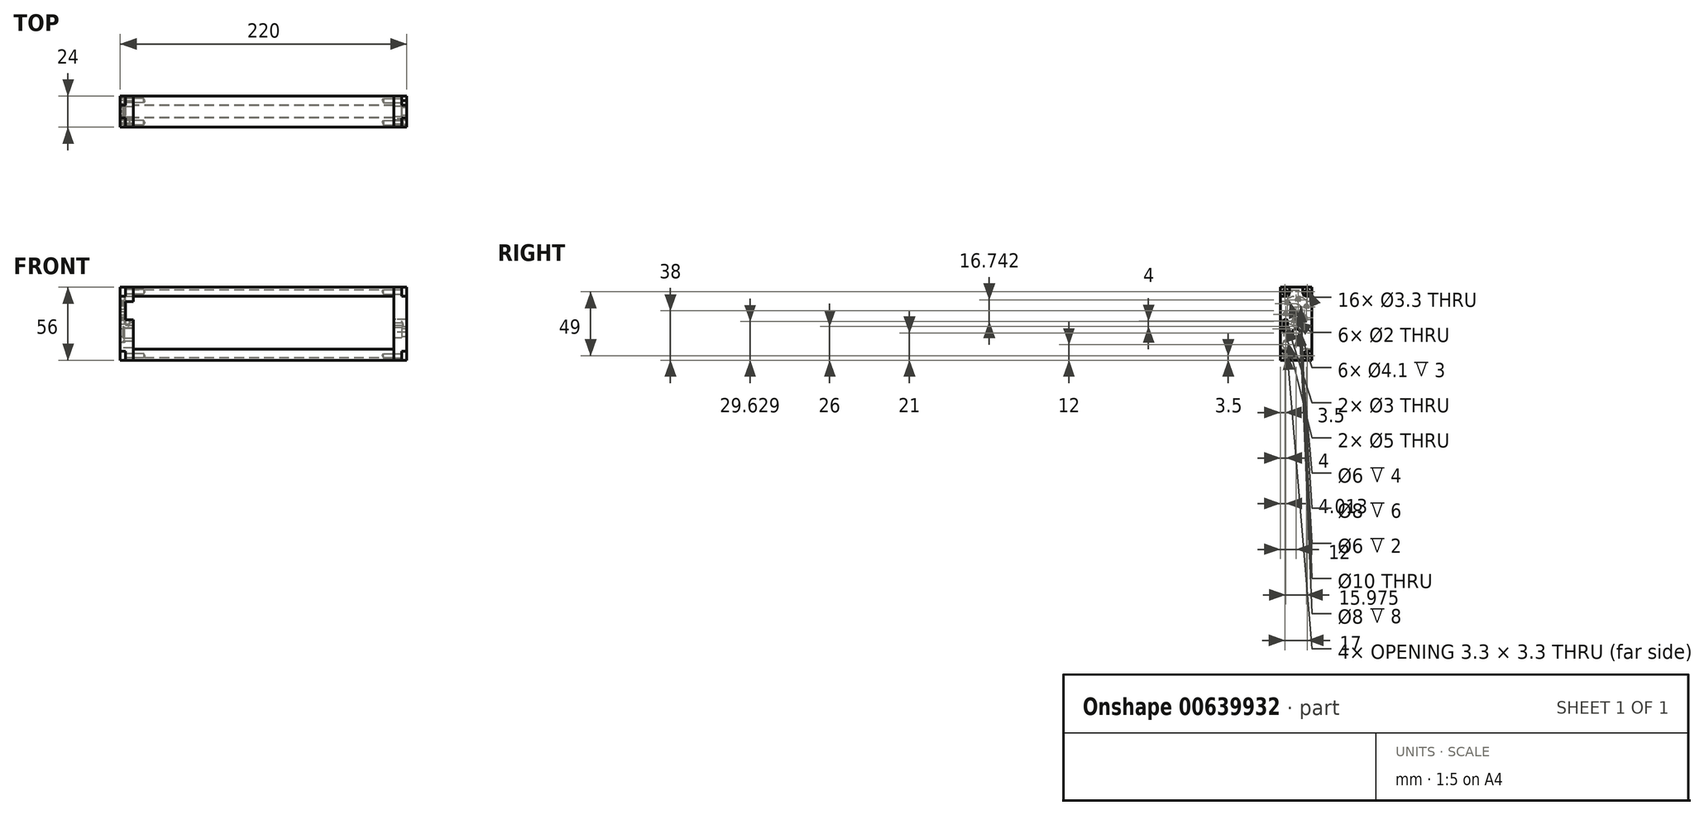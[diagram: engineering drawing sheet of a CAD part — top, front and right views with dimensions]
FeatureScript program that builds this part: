
annotation { "Feature Type Name" : "Feature", "Feature Type Description" : "" }
export const myFeature = defineFeature(function(context is Context, id is Id, definition is map)
    precondition{}
    {
        {
            var Q0;
            Q0=qCreatedBy(makeId("Right.planeOp"),FACE);
            var sketch = newSketch(context, id + "F0", { "sketchPlane" : qUnion([Q0])});
            skLineSegment(sketch, "E0.bottom", {"start": v(0, 0) * mm, "end": v(24, 0) * mm});
            skLineSegment(sketch, "E0.top", {"start": v(0, 56) * mm, "end": v(24, 56) * mm});
            skLineSegment(sketch, "E0.left", {"start": v(0, 0) * mm, "end": v(0, 56) * mm});
            skLineSegment(sketch, "E0.right", {"start": v(24, 0) * mm, "end": v(24, 56) * mm});
            skCircle(sketch, "E1", {"center": v(12, 38) * mm, "radius": 5 * mm});
            skCircle(sketch, "E2", {"center": v(12, 21) * mm, "radius": 3 * mm});
            skLineSegment(sketch, "E3", {"start": v(12, 56) * mm, "end": v(12, 0) * mm, "construction": true});
            skCircle(sketch, "E4", {"center": v(4, 12) * mm, "radius": 2.5 * mm});
            skCircle(sketch, "E5", {"center": v(4, 26) * mm, "radius": 1.5 * mm});
            skSolve(sketch);
        }
        {
            var Q0;
            Q0 = qSketchRegion(id + "F0", true);
            extrude(context, id + "F1", {"entities" : qUnion([Q0]), "depth" : 10 * mm, "offsetDistance" : 25 * mm});
        }
        {
            var Q0;
            Q0=makeQuery(id+"F1.opExtrude","CAP_FACE",FACE,{"disambiguationData":[OSD([sQuery(id+"F0.wireOp",EDGE,"E0.bottom"),sQuery(id+"F0.wireOp",EDGE,"E0.top"),sQuery(id+"F0.wireOp",EDGE,"E0.left"),sQuery(id+"F0.wireOp",EDGE,"E0.right"),sQuery(id+"F0.wireOp",EDGE,"E1"),sQuery(id+"F0.wireOp",EDGE,"E2")])],"isStart":false});
            var sketch = newSketch(context, id + "F2", { "sketchPlane" : qUnion([Q0])});
            skCircle(sketch, "E6", {"center": v(12, 38) * mm, "radius": 11.1 * mm});
            skSolve(sketch);
        }
        {
            var Q0;
            Q0 = qSketchRegion(id + "F2", true);
            extrude(context, id + "F3", {"entities" : qUnion([Q0]), "operationType" : NewBodyOperationType.REMOVE, "oppositeDirection" : true, "depth" : 6 * mm, "offsetDistance" : 25 * mm});
        }
        {
            var Q0;
            Q0=makeQuery(id+"F1.opExtrude","CAP_FACE",FACE,{"disambiguationData":[OSD([sQuery(id+"F0.wireOp",EDGE,"E0.bottom"),sQuery(id+"F0.wireOp",EDGE,"E0.top"),sQuery(id+"F0.wireOp",EDGE,"E0.left"),sQuery(id+"F0.wireOp",EDGE,"E0.right"),sQuery(id+"F0.wireOp",EDGE,"E1"),sQuery(id+"F0.wireOp",EDGE,"E2")])],"isStart":false});
            var sketch = newSketch(context, id + "F4", { "sketchPlane" : qUnion([Q0])});
            skCircle(sketch, "E7", {"center": v(12, 21) * mm, "radius": 4 * mm});
            skSolve(sketch);
        }
        {
            var Q0;
            Q0=makeQuery(id+"F4.imprint","IMPRINT",FACE,{"disambiguationData":[TD([[makeQuery(id+"F4.imprint","IMPRINT",EDGE,{"derivedFrom":sQuery(id+"F4.wireOp",EDGE,"E7")}),1.0]])]});
            extrude(context, id + "F5", {"entities" : qUnion([Q0]), "operationType" : NewBodyOperationType.REMOVE, "oppositeDirection" : true, "depth" : 8 * mm, "offsetDistance" : 25 * mm});
        }
        {
            var Q0;
            Q0=makeQuery(id+"F1.opExtrude","CAP_FACE",FACE,{"disambiguationData":[OSD([sQuery(id+"F0.wireOp",EDGE,"E0.bottom"),sQuery(id+"F0.wireOp",EDGE,"E0.top"),sQuery(id+"F0.wireOp",EDGE,"E0.left"),sQuery(id+"F0.wireOp",EDGE,"E0.right"),sQuery(id+"F0.wireOp",EDGE,"E1"),sQuery(id+"F0.wireOp",EDGE,"E2")])],"isStart":true});
            var sketch = newSketch(context, id + "F6", { "sketchPlane" : qUnion([Q0])});
            skCircle(sketch, "E8.cCircle", {"center": v(-12, 38) * mm, "radius": 8.5 * mm, "construction": true});
            skLineSegment(sketch, "E8.0", {"start": v(-19.99, 40.9) * mm, "end": v(-13.48, 46.37) * mm, "construction": true});
            skLineSegment(sketch, "E8.1", {"start": v(-13.48, 46.37) * mm, "end": v(-5.49, 43.46) * mm, "construction": true});
            skLineSegment(sketch, "E8.2", {"start": v(-5.49, 43.46) * mm, "end": v(-4.01, 35.1) * mm, "construction": true});
            skLineSegment(sketch, "E8.3", {"start": v(-4.01, 35.1) * mm, "end": v(-10.52, 29.63) * mm, "construction": true});
            skLineSegment(sketch, "E8.4", {"start": v(-10.52, 29.63) * mm, "end": v(-18.51, 32.54) * mm, "construction": true});
            skLineSegment(sketch, "E8.5", {"start": v(-18.51, 32.54) * mm, "end": v(-19.99, 40.9) * mm, "construction": true});
            skLineSegment(sketch, "E9", {"start": v(-10.52, 29.63) * mm, "end": v(-13.48, 46.37) * mm, "construction": true});
            skPoint(sketch, "E10", {"position": v(-19.99, 40.9) * mm});
            skPoint(sketch, "E11", {"position": v(-18.51, 32.54) * mm});
            skPoint(sketch, "E12", {"position": v(-10.52, 29.63) * mm});
            skPoint(sketch, "E13", {"position": v(-4.01, 35.1) * mm});
            skPoint(sketch, "E14", {"position": v(-5.49, 43.46) * mm});
            skPoint(sketch, "E15", {"position": v(-13.48, 46.37) * mm});
            skLineSegment(sketch, "E16", {"start": v(-12, 38) * mm, "end": v(-12, 0) * mm, "construction": true});
            skSolve(sketch);
        }
        {
            var Q0;
            Q0=sQuery(id+"F6.wireOp",VERTEX,"E15");
            var Q1;
            Q1=sQuery(id+"F6.wireOp",VERTEX,"E10");
            var Q2;
            Q2=sQuery(id+"F6.wireOp",VERTEX,"E11");
            var Q3;
            Q3=sQuery(id+"F6.wireOp",VERTEX,"E12");
            var Q4;
            Q4=sQuery(id+"F6.wireOp",VERTEX,"E13");
            var Q5;
            Q5=sQuery(id+"F6.wireOp",VERTEX,"E14");
            var Q6;
            Q6=makeQuery(id+"F1.opExtrude","SWEPT_BODY",BODY,{"disambiguationData":[OSD([sQuery(id+"F0.wireOp",EDGE,"E0.bottom"),sQuery(id+"F0.wireOp",EDGE,"E0.top"),sQuery(id+"F0.wireOp",EDGE,"E0.left"),sQuery(id+"F0.wireOp",EDGE,"E0.right"),sQuery(id+"F0.wireOp",EDGE,"E1"),sQuery(id+"F0.wireOp",EDGE,"E2")])]});
            hole(context, id + "F7", {"style" : HoleStyle.C_BORE, "endStyle" : HoleEndStyle.BLIND, "holeDiameter" : 2 * mm, "cBoreDiameter" : 4.1 * mm, "cBoreDepth" : 3 * mm, "majorDiameter" : 5 * mm, "holeDepth" : 10 * mm, "isTappedThrough" : true, "tappedDepth" : 7 * mm, "tapClearance" : 2, "startFromSketch" : true, "locations" : qUnion([Q0, Q1, Q2, Q3, Q4, Q5]), "scope" : qUnion([Q6])});
        }
        {
            var Q0;
            Q0=makeQuery(id+"F3.boolean.opBoolean","COPY",FACE,{"derivedFrom":makeQuery(id+"F3.opExtrude","CAP_FACE",FACE,{"disambiguationData":[OSD([sQuery(id+"F2.wireOp",EDGE,"E6")])],"isStart":false})});
            var sketch = newSketch(context, id + "F8", { "sketchPlane" : qUnion([Q0])});
            skLineSegment(sketch, "E17.bottom", {"start": v(0, 45) * mm, "end": v(24, 45) * mm});
            skLineSegment(sketch, "E17.top", {"start": v(0, 31) * mm, "end": v(24, 31) * mm});
            skLineSegment(sketch, "E17.left", {"start": v(0, 45) * mm, "end": v(0, 31) * mm});
            skLineSegment(sketch, "E17.right", {"start": v(24, 45) * mm, "end": v(24, 31) * mm});
            skLineSegment(sketch, "E18", {"start": v(12, 38) * mm, "end": v(34.16, 38) * mm, "construction": true});
            skPoint(sketch, "E18.endSnap0", {"position": v(24, 38) * mm});
            skSolve(sketch);
        }
        {
            var Q0;
            Q0 = qSketchRegion(id + "F8", true);
            extrude(context, id + "F9", {"entities" : qUnion([Q0]), "operationType" : NewBodyOperationType.REMOVE, "depth" : 25 * mm, "offsetDistance" : 25 * mm});
        }
        {
            var Q0;
            {var subQ0=sQuery(id+"F0.wireOp",EDGE,"E0.right");var subQ1=sQuery(id+"F0.wireOp",EDGE,"E0.left");var subQ2=sQuery(id+"F0.wireOp",EDGE,"E0.bottom");Q0=makeQuery(id+"F9.boolean.opBoolean","SPLIT",FACE,{"disambiguationData":[TD([makeQuery(id+"F1.opExtrude","SWEPT_FACE",FACE,{"disambiguationData":[OSD([subQ2])]})])],"derivedFrom":makeQuery(id+"F1.opExtrude","CAP_FACE",FACE,{"disambiguationData":[OSD([subQ2,sQuery(id+"F0.wireOp",EDGE,"E0.top"),subQ1,subQ0,sQuery(id+"F0.wireOp",EDGE,"E1"),sQuery(id+"F0.wireOp",EDGE,"E2")])],"isStart":false})});}
            var sketch = newSketch(context, id + "F10", { "sketchPlane" : qUnion([Q0])});
            skLineSegment(sketch, "E19.bottom", {"start": v(0, 0) * mm, "end": v(24, 0) * mm});
            skLineSegment(sketch, "E19.top", {"start": v(0, 2) * mm, "end": v(24, 2) * mm});
            skLineSegment(sketch, "E19.left", {"start": v(0, 0) * mm, "end": v(0, 2) * mm});
            skLineSegment(sketch, "E19.right", {"start": v(24, 0) * mm, "end": v(24, 2) * mm});
            skLineSegment(sketch, "E20.bottom", {"start": v(0, 2) * mm, "end": v(7.5, 2) * mm});
            skLineSegment(sketch, "E20.top", {"start": v(0, 8.5) * mm, "end": v(7.5, 8.5) * mm});
            skLineSegment(sketch, "E20.left", {"start": v(0, 2) * mm, "end": v(0, 8.5) * mm});
            skLineSegment(sketch, "E20.right", {"start": v(7.5, 2) * mm, "end": v(7.5, 8.5) * mm});
            skLineSegment(sketch, "E21.bottom", {"start": v(24, 2) * mm, "end": v(16.5, 2) * mm});
            skLineSegment(sketch, "E21.top", {"start": v(24, 8.5) * mm, "end": v(16.5, 8.5) * mm});
            skLineSegment(sketch, "E21.left", {"start": v(24, 2) * mm, "end": v(24, 8.5) * mm});
            skLineSegment(sketch, "E21.right", {"start": v(16.5, 2) * mm, "end": v(16.5, 8.5) * mm});
            skLineSegment(sketch, "E22.bottom", {"start": v(0, 56) * mm, "end": v(24, 56) * mm});
            skLineSegment(sketch, "E22.top", {"start": v(0, 54) * mm, "end": v(24, 54) * mm});
            skLineSegment(sketch, "E22.left", {"start": v(0, 56) * mm, "end": v(0, 54) * mm});
            skLineSegment(sketch, "E22.right", {"start": v(24, 56) * mm, "end": v(24, 54) * mm});
            skLineSegment(sketch, "E23.bottom", {"start": v(0, 54) * mm, "end": v(7, 54) * mm});
            skLineSegment(sketch, "E23.top", {"start": v(0, 49) * mm, "end": v(7, 49) * mm});
            skLineSegment(sketch, "E23.left", {"start": v(0, 54) * mm, "end": v(0, 49) * mm});
            skLineSegment(sketch, "E23.right", {"start": v(7, 54) * mm, "end": v(7, 49) * mm});
            skLineSegment(sketch, "E24.bottom", {"start": v(24, 54) * mm, "end": v(17, 54) * mm});
            skLineSegment(sketch, "E24.top", {"start": v(24, 49) * mm, "end": v(17, 49) * mm});
            skLineSegment(sketch, "E24.left", {"start": v(24, 54) * mm, "end": v(24, 49) * mm});
            skLineSegment(sketch, "E24.right", {"start": v(17, 54) * mm, "end": v(17, 49) * mm});
            skSolve(sketch);
        }
        {
            var Q0;
            Q0 = qSketchRegion(id + "F10", true);
            extrude(context, id + "F11", {"entities" : qUnion([Q0]), "depth" : 200 * mm, "offsetDistance" : 25 * mm});
        }
        {
            var Q0;
            Q0=qCreatedBy(makeId("Right.planeOp"),FACE);
            var sketch = newSketch(context, id + "F12", { "sketchPlane" : qUnion([Q0])});
            skLineSegment(sketch, "E25.bottom", {"start": v(20.5, 52.5) * mm, "end": v(3.5, 52.5) * mm, "construction": true});
            skLineSegment(sketch, "E25.top", {"start": v(20.5, 3.5) * mm, "end": v(3.5, 3.5) * mm, "construction": true});
            skLineSegment(sketch, "E25.left", {"start": v(20.5, 52.5) * mm, "end": v(20.5, 3.5) * mm, "construction": true});
            skLineSegment(sketch, "E25.right", {"start": v(3.5, 52.5) * mm, "end": v(3.5, 3.5) * mm, "construction": true});
            skPoint(sketch, "E26", {"position": v(20.5, 52.5) * mm});
            skPoint(sketch, "E27", {"position": v(3.5, 52.5) * mm});
            skPoint(sketch, "E28", {"position": v(3.5, 3.5) * mm});
            skPoint(sketch, "E29", {"position": v(20.5, 3.5) * mm});
            skSolve(sketch);
        }
        {
            var Q0;
            Q0=sQuery(id+"F12.wireOp",VERTEX,"E26");
            var Q1;
            Q1=sQuery(id+"F12.wireOp",VERTEX,"E27");
            var Q2;
            Q2=sQuery(id+"F12.wireOp",VERTEX,"E29");
            var Q3;
            Q3=sQuery(id+"F12.wireOp",VERTEX,"E28");
            var Q4;
            Q4=makeQuery(id+"F1.opExtrude","SWEPT_BODY",BODY,{"disambiguationData":[OSD([sQuery(id+"F0.wireOp",EDGE,"E0.bottom"),sQuery(id+"F0.wireOp",EDGE,"E0.top"),sQuery(id+"F0.wireOp",EDGE,"E0.left"),sQuery(id+"F0.wireOp",EDGE,"E0.right"),sQuery(id+"F0.wireOp",EDGE,"E1"),sQuery(id+"F0.wireOp",EDGE,"E2")])]});
            var Q5;
            Q5=makeQuery(id+"F11.opExtrude","SWEPT_BODY",BODY,{"disambiguationData":[OSD([sQuery(id+"F10.wireOp",EDGE,"E22.bottom"),sQuery(id+"F10.wireOp",EDGE,"E22.top"),sQuery(id+"F10.wireOp",EDGE,"E22.left"),sQuery(id+"F10.wireOp",EDGE,"E22.right"),sQuery(id+"F10.wireOp",EDGE,"E23.top"),sQuery(id+"F10.wireOp",EDGE,"E23.left"),sQuery(id+"F10.wireOp",EDGE,"E23.right"),sQuery(id+"F10.wireOp",EDGE,"E24.top"),sQuery(id+"F10.wireOp",EDGE,"E24.left"),sQuery(id+"F10.wireOp",EDGE,"E24.right")])]});
            var Q6;
            Q6=makeQuery(id+"F11.opExtrude","SWEPT_BODY",BODY,{"disambiguationData":[OSD([sQuery(id+"F10.wireOp",EDGE,"E19.bottom"),sQuery(id+"F10.wireOp",EDGE,"E19.top"),sQuery(id+"F10.wireOp",EDGE,"E19.left"),sQuery(id+"F10.wireOp",EDGE,"E19.right"),sQuery(id+"F10.wireOp",EDGE,"E20.top"),sQuery(id+"F10.wireOp",EDGE,"E20.left"),sQuery(id+"F10.wireOp",EDGE,"E20.right"),sQuery(id+"F10.wireOp",EDGE,"E21.top"),sQuery(id+"F10.wireOp",EDGE,"E21.left"),sQuery(id+"F10.wireOp",EDGE,"E21.right")])]});
            hole(context, id + "F13", {"style" : HoleStyle.SIMPLE, "endStyle" : HoleEndStyle.BLIND, "oppositeDirection" : true, "standardTappedOrClearance" : lookupTablePath({ "standard" : "ISO", "fit" : "Normal", "size" : "M3", "type" : "Clearance" }), "standardBlindInLast" : lookupTablePath({ "fit" : "Standard", "standard" : "ISO", "size" : "M3", "type" : "Clearance" }), "holeDiameter" : 3.3 * mm, "majorDiameter" : 5 * mm, "holeDepth" : 18 * mm, "isTappedThrough" : true, "tappedDepth" : 7 * mm, "tapClearance" : 2, "startFromSketch" : true, "locations" : qUnion([Q0, Q1, Q2, Q3]), "scope" : qUnion([Q4, Q5, Q6])});
        }
        {
            var Q0;
            Q0=makeQuery(id+"F1.opExtrude","CAP_FACE",FACE,{"disambiguationData":[OSD([sQuery(id+"F0.wireOp",EDGE,"E0.bottom"),sQuery(id+"F0.wireOp",EDGE,"E0.top"),sQuery(id+"F0.wireOp",EDGE,"E0.left"),sQuery(id+"F0.wireOp",EDGE,"E0.right"),sQuery(id+"F0.wireOp",EDGE,"E1"),sQuery(id+"F0.wireOp",EDGE,"E2")])],"isStart":true});
            var sketch = newSketch(context, id + "F14", { "sketchPlane" : qUnion([Q0])});
            skCircle(sketch, "E30", {"center": v(-20.5, 52.5) * mm, "radius": 3.5 * mm});
            skCircle(sketch, "E31", {"center": v(-3.5, 52.5) * mm, "radius": 3.5 * mm});
            skCircle(sketch, "E32", {"center": v(-3.5, 3.5) * mm, "radius": 3.5 * mm});
            skCircle(sketch, "E33", {"center": v(-20.5, 3.5) * mm, "radius": 3.5 * mm});
            skLineSegment(sketch, "E34", {"start": v(-17, 52.5) * mm, "end": v(-17, 56) * mm});
            skLineSegment(sketch, "E35", {"start": v(-17, 56) * mm, "end": v(-24, 56) * mm});
            skLineSegment(sketch, "E36", {"start": v(-24, 56) * mm, "end": v(-24, 49) * mm});
            skLineSegment(sketch, "E37", {"start": v(-24, 49) * mm, "end": v(-20.5, 49) * mm});
            skLineSegment(sketch, "E38", {"start": v(-7, 52.5) * mm, "end": v(-7, 56) * mm});
            skLineSegment(sketch, "E39", {"start": v(-7, 56) * mm, "end": v(0, 56) * mm});
            skLineSegment(sketch, "E40", {"start": v(0, 56) * mm, "end": v(0, 49) * mm});
            skLineSegment(sketch, "E41", {"start": v(0, 49) * mm, "end": v(-3.5, 49) * mm});
            skLineSegment(sketch, "E42", {"start": v(-20.5, 7) * mm, "end": v(-24, 7) * mm});
            skLineSegment(sketch, "E43", {"start": v(-24, 7) * mm, "end": v(-24, 0) * mm});
            skLineSegment(sketch, "E44", {"start": v(-24, 0) * mm, "end": v(-17, 0) * mm});
            skLineSegment(sketch, "E45", {"start": v(-17, 0) * mm, "end": v(-17, 3.5) * mm});
            skLineSegment(sketch, "E46", {"start": v(-7, 3.5) * mm, "end": v(-7, 0) * mm});
            skLineSegment(sketch, "E47", {"start": v(-7, 0) * mm, "end": v(0, 0) * mm});
            skLineSegment(sketch, "E48", {"start": v(0, 0) * mm, "end": v(0, 7) * mm});
            skLineSegment(sketch, "E49", {"start": v(0, 7) * mm, "end": v(-3.5, 7) * mm});
            skSolve(sketch);
        }
        {
            var Q0;
            Q0 = qSketchRegion(id + "F14", true);
            extrude(context, id + "F15", {"entities" : qUnion([Q0]), "operationType" : NewBodyOperationType.REMOVE, "oppositeDirection" : true, "depth" : 4 * mm, "offsetDistance" : 25 * mm});
        }
        {
            var Q0;
            Q0=makeQuery(id+"F11.opExtrude","CAP_FACE",FACE,{"disambiguationData":[OSD([sQuery(id+"F10.wireOp",EDGE,"E19.bottom"),sQuery(id+"F10.wireOp",EDGE,"E19.top"),sQuery(id+"F10.wireOp",EDGE,"E19.left"),sQuery(id+"F10.wireOp",EDGE,"E19.right"),sQuery(id+"F10.wireOp",EDGE,"E20.top"),sQuery(id+"F10.wireOp",EDGE,"E20.left"),sQuery(id+"F10.wireOp",EDGE,"E20.right"),sQuery(id+"F10.wireOp",EDGE,"E21.top"),sQuery(id+"F10.wireOp",EDGE,"E21.left"),sQuery(id+"F10.wireOp",EDGE,"E21.right")])],"isStart":false});
            var sketch = newSketch(context, id + "F16", { "sketchPlane" : qUnion([Q0])});
            skLineSegment(sketch, "E50.bottom", {"start": v(0, 0) * mm, "end": v(24, 0) * mm});
            skLineSegment(sketch, "E50.top", {"start": v(0, 56) * mm, "end": v(24, 56) * mm});
            skLineSegment(sketch, "E50.left", {"start": v(0, 0) * mm, "end": v(0, 56) * mm});
            skLineSegment(sketch, "E50.right", {"start": v(24, 0) * mm, "end": v(24, 56) * mm});
            skCircle(sketch, "E51", {"center": v(12, 21) * mm, "radius": 3 * mm});
            skLineSegment(sketch, "E52", {"start": v(12, 56) * mm, "end": v(12, 0) * mm, "construction": true});
            skCircle(sketch, "E53", {"center": v(4, 24) * mm, "radius": 2.5 * mm});
            skCircle(sketch, "E54", {"center": v(4, 30) * mm, "radius": 1.5 * mm});
            skSolve(sketch);
        }
        {
            var Q0;
            Q0 = qSketchRegion(id + "F16", true);
            extrude(context, id + "F17", {"entities" : qUnion([Q0]), "depth" : 10 * mm, "offsetDistance" : 25 * mm});
        }
        {
            var Q0;
            Q0=makeQuery(id+"F17.opExtrude","CAP_FACE",FACE,{"disambiguationData":[OSD([sQuery(id+"F16.wireOp",EDGE,"E50.bottom"),sQuery(id+"F16.wireOp",EDGE,"E50.top"),sQuery(id+"F16.wireOp",EDGE,"E50.left"),sQuery(id+"F16.wireOp",EDGE,"E50.right"),sQuery(id+"F16.wireOp",EDGE,"E51"),sQuery(id+"F16.wireOp",EDGE,"etqKSdQV-xPis-J3Dk-ImyQ-uri6VPnfRBX9.bottom"),sQuery(id+"F16.wireOp",EDGE,"etqKSdQV-xPis-J3Dk-ImyQ-uri6VPnfRBX9.top"),sQuery(id+"F16.wireOp",EDGE,"etqKSdQV-xPis-J3Dk-ImyQ-uri6VPnfRBX9.left"),sQuery(id+"F16.wireOp",EDGE,"etqKSdQV-xPis-J3Dk-ImyQ-uri6VPnfRBX9.right")])],"isStart":false});
            var sketch = newSketch(context, id + "F18", { "sketchPlane" : qUnion([Q0])});
            skLineSegment(sketch, "E55.bottom", {"start": v(3.5, 52.5) * mm, "end": v(20.5, 52.5) * mm, "construction": true});
            skLineSegment(sketch, "E55.top", {"start": v(3.5, 3.5) * mm, "end": v(20.5, 3.5) * mm, "construction": true});
            skLineSegment(sketch, "E55.left", {"start": v(3.5, 52.5) * mm, "end": v(3.5, 3.5) * mm, "construction": true});
            skLineSegment(sketch, "E55.right", {"start": v(20.5, 52.5) * mm, "end": v(20.5, 3.5) * mm, "construction": true});
            skPoint(sketch, "E56", {"position": v(3.5, 52.5) * mm});
            skPoint(sketch, "E57", {"position": v(20.5, 52.5) * mm});
            skPoint(sketch, "E58", {"position": v(20.5, 3.5) * mm});
            skPoint(sketch, "E59", {"position": v(3.5, 3.5) * mm});
            skSolve(sketch);
        }
        {
            var Q0;
            Q0=sQuery(id+"F18.wireOp",VERTEX,"E55.bottom.start");
            var Q1;
            Q1=sQuery(id+"F18.wireOp",VERTEX,"E55.right.start");
            var Q2;
            Q2=sQuery(id+"F18.wireOp",VERTEX,"E58");
            var Q3;
            Q3=sQuery(id+"F18.wireOp",VERTEX,"E59");
            var Q4;
            Q4=makeQuery(id+"F11.opExtrude","SWEPT_BODY",BODY,{"disambiguationData":[OSD([sQuery(id+"F10.wireOp",EDGE,"E19.bottom"),sQuery(id+"F10.wireOp",EDGE,"E19.top"),sQuery(id+"F10.wireOp",EDGE,"E19.left"),sQuery(id+"F10.wireOp",EDGE,"E19.right"),sQuery(id+"F10.wireOp",EDGE,"E20.top"),sQuery(id+"F10.wireOp",EDGE,"E20.left"),sQuery(id+"F10.wireOp",EDGE,"E20.right"),sQuery(id+"F10.wireOp",EDGE,"E21.top"),sQuery(id+"F10.wireOp",EDGE,"E21.left"),sQuery(id+"F10.wireOp",EDGE,"E21.right")])]});
            var Q5;
            Q5=makeQuery(id+"F11.opExtrude","SWEPT_BODY",BODY,{"disambiguationData":[OSD([sQuery(id+"F10.wireOp",EDGE,"E22.bottom"),sQuery(id+"F10.wireOp",EDGE,"E22.top"),sQuery(id+"F10.wireOp",EDGE,"E22.left"),sQuery(id+"F10.wireOp",EDGE,"E22.right"),sQuery(id+"F10.wireOp",EDGE,"E23.top"),sQuery(id+"F10.wireOp",EDGE,"E23.left"),sQuery(id+"F10.wireOp",EDGE,"E23.right"),sQuery(id+"F10.wireOp",EDGE,"E24.top"),sQuery(id+"F10.wireOp",EDGE,"E24.left"),sQuery(id+"F10.wireOp",EDGE,"E24.right")])]});
            var Q6;
            Q6=makeQuery(id+"F17.opExtrude","SWEPT_BODY",BODY,{"disambiguationData":[OSD([sQuery(id+"F16.wireOp",EDGE,"E50.bottom"),sQuery(id+"F16.wireOp",EDGE,"E50.top"),sQuery(id+"F16.wireOp",EDGE,"E50.left"),sQuery(id+"F16.wireOp",EDGE,"E50.right"),sQuery(id+"F16.wireOp",EDGE,"E51"),sQuery(id+"F16.wireOp",EDGE,"etqKSdQV-xPis-J3Dk-ImyQ-uri6VPnfRBX9.bottom"),sQuery(id+"F16.wireOp",EDGE,"etqKSdQV-xPis-J3Dk-ImyQ-uri6VPnfRBX9.top"),sQuery(id+"F16.wireOp",EDGE,"etqKSdQV-xPis-J3Dk-ImyQ-uri6VPnfRBX9.left"),sQuery(id+"F16.wireOp",EDGE,"etqKSdQV-xPis-J3Dk-ImyQ-uri6VPnfRBX9.right")])]});
            hole(context, id + "F19", {"style" : HoleStyle.SIMPLE, "endStyle" : HoleEndStyle.BLIND, "standardTappedOrClearance" : lookupTablePath({ "standard" : "ISO", "fit" : "Normal", "size" : "M3", "type" : "Clearance" }), "standardBlindInLast" : lookupTablePath({ "fit" : "Standard", "standard" : "ISO", "size" : "M3", "type" : "Clearance" }), "holeDiameter" : 3.3 * mm, "majorDiameter" : 5 * mm, "holeDepth" : 18 * mm, "isTappedThrough" : true, "tappedDepth" : 7 * mm, "tapClearance" : 2, "startFromSketch" : true, "locations" : qUnion([Q0, Q1, Q2, Q3]), "scope" : qUnion([Q4, Q5, Q6])});
        }
        {
            var Q0;
            Q0=makeQuery(id+"F17.opExtrude","CAP_FACE",FACE,{"disambiguationData":[OSD([sQuery(id+"F16.wireOp",EDGE,"E50.bottom"),sQuery(id+"F16.wireOp",EDGE,"E50.top"),sQuery(id+"F16.wireOp",EDGE,"E50.left"),sQuery(id+"F16.wireOp",EDGE,"E50.right"),sQuery(id+"F16.wireOp",EDGE,"E51"),sQuery(id+"F16.wireOp",EDGE,"etqKSdQV-xPis-J3Dk-ImyQ-uri6VPnfRBX9.bottom"),sQuery(id+"F16.wireOp",EDGE,"etqKSdQV-xPis-J3Dk-ImyQ-uri6VPnfRBX9.top"),sQuery(id+"F16.wireOp",EDGE,"etqKSdQV-xPis-J3Dk-ImyQ-uri6VPnfRBX9.left"),sQuery(id+"F16.wireOp",EDGE,"etqKSdQV-xPis-J3Dk-ImyQ-uri6VPnfRBX9.right")])],"isStart":false});
            var sketch = newSketch(context, id + "F20", { "sketchPlane" : qUnion([Q0])});
            skCircle(sketch, "E60", {"center": v(3.5, 52.5) * mm, "radius": 3.5 * mm});
            skCircle(sketch, "E61", {"center": v(20.5, 52.5) * mm, "radius": 3.5 * mm});
            skCircle(sketch, "E62", {"center": v(20.5, 3.5) * mm, "radius": 3.5 * mm});
            skCircle(sketch, "E63", {"center": v(3.5, 3.5) * mm, "radius": 3.5 * mm});
            skLineSegment(sketch, "E64", {"start": v(7, 52.5) * mm, "end": v(7, 56) * mm});
            skLineSegment(sketch, "E65", {"start": v(7, 56) * mm, "end": v(0, 56) * mm});
            skLineSegment(sketch, "E66", {"start": v(0, 56) * mm, "end": v(0, 49) * mm});
            skLineSegment(sketch, "E67", {"start": v(0, 49) * mm, "end": v(3.5, 49) * mm});
            skLineSegment(sketch, "E68", {"start": v(17, 52.5) * mm, "end": v(17, 56) * mm});
            skLineSegment(sketch, "E69", {"start": v(17, 56) * mm, "end": v(24, 56) * mm});
            skLineSegment(sketch, "E70", {"start": v(24, 56) * mm, "end": v(24, 49) * mm});
            skLineSegment(sketch, "E71", {"start": v(24, 49) * mm, "end": v(20.4, 49) * mm});
            skLineSegment(sketch, "E72", {"start": v(3.5, 7) * mm, "end": v(0, 7) * mm});
            skLineSegment(sketch, "E73", {"start": v(0, 7) * mm, "end": v(0, 0) * mm});
            skLineSegment(sketch, "E74", {"start": v(0, 0) * mm, "end": v(7, 0) * mm});
            skLineSegment(sketch, "E75", {"start": v(7, 0) * mm, "end": v(7, 3.5) * mm});
            skLineSegment(sketch, "E76", {"start": v(17, 3.5) * mm, "end": v(17, 0) * mm});
            skLineSegment(sketch, "E77", {"start": v(17, 0) * mm, "end": v(24, 0) * mm});
            skLineSegment(sketch, "E78", {"start": v(24, 0) * mm, "end": v(24, 7) * mm});
            skLineSegment(sketch, "E79", {"start": v(24, 7) * mm, "end": v(20.5, 7) * mm});
            skSolve(sketch);
        }
        {
            var Q0;
            Q0 = qSketchRegion(id + "F20", true);
            extrude(context, id + "F21", {"entities" : qUnion([Q0]), "operationType" : NewBodyOperationType.REMOVE, "oppositeDirection" : true, "depth" : 4 * mm, "offsetDistance" : 25 * mm});
        }
        {
            var Q0;
            Q0=makeQuery(id+"F17.opExtrude","CAP_FACE",FACE,{"disambiguationData":[OSD([sQuery(id+"F16.wireOp",EDGE,"E50.bottom"),sQuery(id+"F16.wireOp",EDGE,"E50.top"),sQuery(id+"F16.wireOp",EDGE,"E50.left"),sQuery(id+"F16.wireOp",EDGE,"E50.right"),sQuery(id+"F16.wireOp",EDGE,"E51"),sQuery(id+"F16.wireOp",EDGE,"etqKSdQV-xPis-J3Dk-ImyQ-uri6VPnfRBX9.bottom"),sQuery(id+"F16.wireOp",EDGE,"etqKSdQV-xPis-J3Dk-ImyQ-uri6VPnfRBX9.top"),sQuery(id+"F16.wireOp",EDGE,"etqKSdQV-xPis-J3Dk-ImyQ-uri6VPnfRBX9.left"),sQuery(id+"F16.wireOp",EDGE,"etqKSdQV-xPis-J3Dk-ImyQ-uri6VPnfRBX9.right")])],"isStart":true});
            var sketch = newSketch(context, id + "F22", { "sketchPlane" : qUnion([Q0])});
            skCircle(sketch, "E80", {"center": v(-12, 21) * mm, "radius": 4 * mm});
            skSolve(sketch);
        }
        {
            var Q0;
            Q0 = qSketchRegion(id + "F22", true);
            extrude(context, id + "F23", {"entities" : qUnion([Q0]), "operationType" : NewBodyOperationType.REMOVE, "oppositeDirection" : true, "depth" : 6 * mm, "offsetDistance" : 25 * mm});
        }
        {
            var Q0;
            Q0=makeQuery(id+"F17.opExtrude","CAP_FACE",FACE,{"disambiguationData":[OSD([sQuery(id+"F16.wireOp",EDGE,"E50.bottom"),sQuery(id+"F16.wireOp",EDGE,"E50.top"),sQuery(id+"F16.wireOp",EDGE,"E50.left"),sQuery(id+"F16.wireOp",EDGE,"E50.right"),sQuery(id+"F16.wireOp",EDGE,"E51"),sQuery(id+"F16.wireOp",EDGE,"E53"),sQuery(id+"F16.wireOp",EDGE,"E54")])],"isStart":false});
            var sketch = newSketch(context, id + "F24", { "sketchPlane" : qUnion([Q0])});
            skLineSegment(sketch, "E81.bottom", {"start": v(2.5, 30) * mm, "end": v(5.5, 30) * mm});
            skLineSegment(sketch, "E81.top", {"start": v(2.5, 26) * mm, "end": v(5.5, 26) * mm});
            skLineSegment(sketch, "E81.left", {"start": v(2.5, 30) * mm, "end": v(2.5, 26) * mm});
            skLineSegment(sketch, "E81.right", {"start": v(5.5, 30) * mm, "end": v(5.5, 26) * mm});
            skSolve(sketch);
        }
        {
            var Q0;
            Q0 = qSketchRegion(id + "F24", true);
            extrude(context, id + "F25", {"entities" : qUnion([Q0]), "operationType" : NewBodyOperationType.REMOVE, "oppositeDirection" : true, "depth" : 3 * mm, "offsetDistance" : 25 * mm});
        }
        {
            var Q0;
            Q0=makeQuery(id+"F1.opExtrude","CAP_FACE",FACE,{"disambiguationData":[OSD([sQuery(id+"F0.wireOp",EDGE,"E0.bottom"),sQuery(id+"F0.wireOp",EDGE,"E0.top"),sQuery(id+"F0.wireOp",EDGE,"E0.left"),sQuery(id+"F0.wireOp",EDGE,"E0.right"),sQuery(id+"F0.wireOp",EDGE,"E1"),sQuery(id+"F0.wireOp",EDGE,"E2"),sQuery(id+"F0.wireOp",EDGE,"E4"),sQuery(id+"F0.wireOp",EDGE,"E5")])],"isStart":true});
            var sketch = newSketch(context, id + "F26", { "sketchPlane" : qUnion([Q0])});
            skLineSegment(sketch, "E82.bottom", {"start": v(-5.5, 26) * mm, "end": v(-2.5, 26) * mm});
            skLineSegment(sketch, "E82.top", {"start": v(-5.5, 14) * mm, "end": v(-2.5, 14) * mm});
            skLineSegment(sketch, "E82.left", {"start": v(-5.5, 26) * mm, "end": v(-5.5, 14) * mm});
            skLineSegment(sketch, "E82.right", {"start": v(-2.5, 26) * mm, "end": v(-2.5, 14) * mm});
            skSolve(sketch);
        }
        {
            var Q0;
            Q0 = qSketchRegion(id + "F26", true);
            extrude(context, id + "F27", {"entities" : qUnion([Q0]), "operationType" : NewBodyOperationType.REMOVE, "oppositeDirection" : true, "depth" : 3 * mm, "offsetDistance" : 25 * mm});
        }
        {
            var Q0;
            {var subQ0=sQuery(id+"F0.wireOp",EDGE,"E4");var subQ1=sQuery(id+"F0.wireOp",EDGE,"E0.left");var subQ2=sQuery(id+"F0.wireOp",EDGE,"E0.right");var subQ3=sQuery(id+"F0.wireOp",EDGE,"E0.bottom");var subQ4=sQuery(id+"F0.wireOp",EDGE,"E5");Q0=makeQuery(id+"F9.boolean.opBoolean","SPLIT",FACE,{"disambiguationData":[TD([makeQuery(id+"F1.opExtrude","SWEPT_FACE",FACE,{"disambiguationData":[OSD([subQ3])]})])],"derivedFrom":makeQuery(id+"F1.opExtrude","CAP_FACE",FACE,{"disambiguationData":[OSD([subQ3,sQuery(id+"F0.wireOp",EDGE,"E0.top"),subQ1,subQ2,sQuery(id+"F0.wireOp",EDGE,"E1"),sQuery(id+"F0.wireOp",EDGE,"E2"),subQ0,subQ4])],"isStart":false})});}
            var sketch = newSketch(context, id + "F28", { "sketchPlane" : qUnion([Q0])});
            skLineSegment(sketch, "E83", {"start": v(2.5, 26) * mm, "end": v(2.5, 31) * mm});
            skLineSegment(sketch, "E84", {"start": v(2.5, 31) * mm, "end": v(3.39, 31) * mm});
            skLineSegment(sketch, "E85", {"start": v(3.39, 31) * mm, "end": v(5.5, 29) * mm});
            skLineSegment(sketch, "E86", {"start": v(5.5, 29) * mm, "end": v(5.5, 26) * mm});
            skLineSegment(sketch, "E87", {"start": v(5.5, 26) * mm, "end": v(2.5, 26) * mm});
            skSolve(sketch);
        }
        {
            var Q0;
            Q0 = qSketchRegion(id + "F28", true);
            extrude(context, id + "F29", {"entities" : qUnion([Q0]), "operationType" : NewBodyOperationType.REMOVE, "oppositeDirection" : true, "depth" : 3 * mm, "offsetDistance" : 25 * mm});
        }
        {
            var Q0;
            Q0=makeQuery(id+"F29.boolean.opBoolean","INTERSECT",EDGE,{"derivedFrom":[makeQuery(id+"F1.opExtrude","SWEPT_FACE",FACE,{"disambiguationData":[OSD([sQuery(id+"F0.wireOp",EDGE,"E5")])]}),makeQuery(id+"F29.opExtrude","CAP_FACE",FACE,{"disambiguationData":[OSD([sQuery(id+"F28.wireOp",EDGE,"E83"),sQuery(id+"F28.wireOp",EDGE,"E84"),sQuery(id+"F28.wireOp",EDGE,"E85"),sQuery(id+"F28.wireOp",EDGE,"E86"),sQuery(id+"F28.wireOp",EDGE,"E87")])],"isStart":false})]});
            var Q1;
            Q1=makeQuery(id+"F29.boolean.opBoolean","COPY",EDGE,{"derivedFrom":makeQuery(id+"F29.opExtrude","SWEPT_EDGE",EDGE,{"disambiguationData":[OSD([sQuery(id+"F0.wireOp",EDGE,"E0.bottom"),sQuery(id+"F0.wireOp",EDGE,"E0.top"),sQuery(id+"F0.wireOp",EDGE,"E0.left"),sQuery(id+"F0.wireOp",EDGE,"E0.right"),sQuery(id+"F0.wireOp",EDGE,"E1"),sQuery(id+"F0.wireOp",EDGE,"E2"),sQuery(id+"F0.wireOp",EDGE,"E4"),sQuery(id+"F0.wireOp",EDGE,"E5"),sQuery(id+"F8.wireOp",EDGE,"E17.top"),sQuery(id+"F28.wireOp",EDGE,"E83"),sQuery(id+"F28.wireOp",EDGE,"E84")])]})});
            var Q2;
            Q2=makeQuery(id+"F29.boolean.opBoolean","COPY",EDGE,{"derivedFrom":makeQuery(id+"F29.opExtrude","CAP_EDGE",EDGE,{"disambiguationData":[OSD([sQuery(id+"F28.wireOp",EDGE,"E84")])],"isStart":false})});
            var Q3;
            Q3=makeQuery(id+"F27.boolean.opBoolean","INTERSECT",EDGE,{"derivedFrom":[makeQuery(id+"F1.opExtrude","SWEPT_FACE",FACE,{"disambiguationData":[OSD([sQuery(id+"F0.wireOp",EDGE,"E5")])]}),makeQuery(id+"F27.opExtrude","CAP_FACE",FACE,{"disambiguationData":[OSD([sQuery(id+"F26.wireOp",EDGE,"E82.bottom"),sQuery(id+"F26.wireOp",EDGE,"E82.top"),sQuery(id+"F26.wireOp",EDGE,"E82.left"),sQuery(id+"F26.wireOp",EDGE,"E82.right")])],"isStart":false})]});
            var Q4;
            Q4=makeQuery(id+"F27.boolean.opBoolean","COPY",EDGE,{"derivedFrom":makeQuery(id+"F27.opExtrude","CAP_EDGE",EDGE,{"disambiguationData":[OSD([sQuery(id+"F26.wireOp",EDGE,"E82.left")])],"isStart":false})});
            var Q5;
            Q5=makeQuery(id+"F27.boolean.opBoolean","COPY",EDGE,{"derivedFrom":makeQuery(id+"F27.opExtrude","CAP_EDGE",EDGE,{"disambiguationData":[OSD([sQuery(id+"F26.wireOp",EDGE,"E82.right")])],"isStart":false})});
            var Q6;
            Q6=makeQuery(id+"F27.boolean.opBoolean","INTERSECT",EDGE,{"derivedFrom":[makeQuery(id+"F1.opExtrude","SWEPT_FACE",FACE,{"disambiguationData":[OSD([sQuery(id+"F0.wireOp",EDGE,"E4")])]}),makeQuery(id+"F27.opExtrude","CAP_FACE",FACE,{"disambiguationData":[OSD([sQuery(id+"F26.wireOp",EDGE,"E82.bottom"),sQuery(id+"F26.wireOp",EDGE,"E82.top"),sQuery(id+"F26.wireOp",EDGE,"E82.left"),sQuery(id+"F26.wireOp",EDGE,"E82.right")])],"isStart":false})]});
            var Q7;
            Q7=makeQuery(id+"F25.boolean.opBoolean","INTERSECT",EDGE,{"derivedFrom":[makeQuery(id+"F17.opExtrude","SWEPT_FACE",FACE,{"disambiguationData":[OSD([sQuery(id+"F16.wireOp",EDGE,"E53")])]}),makeQuery(id+"F25.opExtrude","CAP_FACE",FACE,{"disambiguationData":[OSD([sQuery(id+"F24.wireOp",EDGE,"E81.bottom"),sQuery(id+"F24.wireOp",EDGE,"E81.top"),sQuery(id+"F24.wireOp",EDGE,"E81.left"),sQuery(id+"F24.wireOp",EDGE,"E81.right")])],"isStart":false})]});
            var Q8;
            Q8=makeQuery(id+"F25.boolean.opBoolean","INTERSECT",EDGE,{"derivedFrom":[makeQuery(id+"F17.opExtrude","SWEPT_FACE",FACE,{"disambiguationData":[OSD([sQuery(id+"F16.wireOp",EDGE,"E54")])]}),makeQuery(id+"F25.opExtrude","CAP_FACE",FACE,{"disambiguationData":[OSD([sQuery(id+"F24.wireOp",EDGE,"E81.bottom"),sQuery(id+"F24.wireOp",EDGE,"E81.top"),sQuery(id+"F24.wireOp",EDGE,"E81.left"),sQuery(id+"F24.wireOp",EDGE,"E81.right")])],"isStart":false})]});
            var Q9;
            Q9=makeQuery(id+"F17.opExtrude","CAP_EDGE",EDGE,{"disambiguationData":[OSD([sQuery(id+"F16.wireOp",EDGE,"E54")])],"isStart":true});
            fillet(context, id + "F30", {"entities" : qUnion([Q0, Q1, Q2, Q3, Q4, Q5, Q6, Q7, Q8, Q9]), "radius" : 1 * mm, "tangentPropagation" : true, "allowEdgeOverflow" : false});
        }
    });
